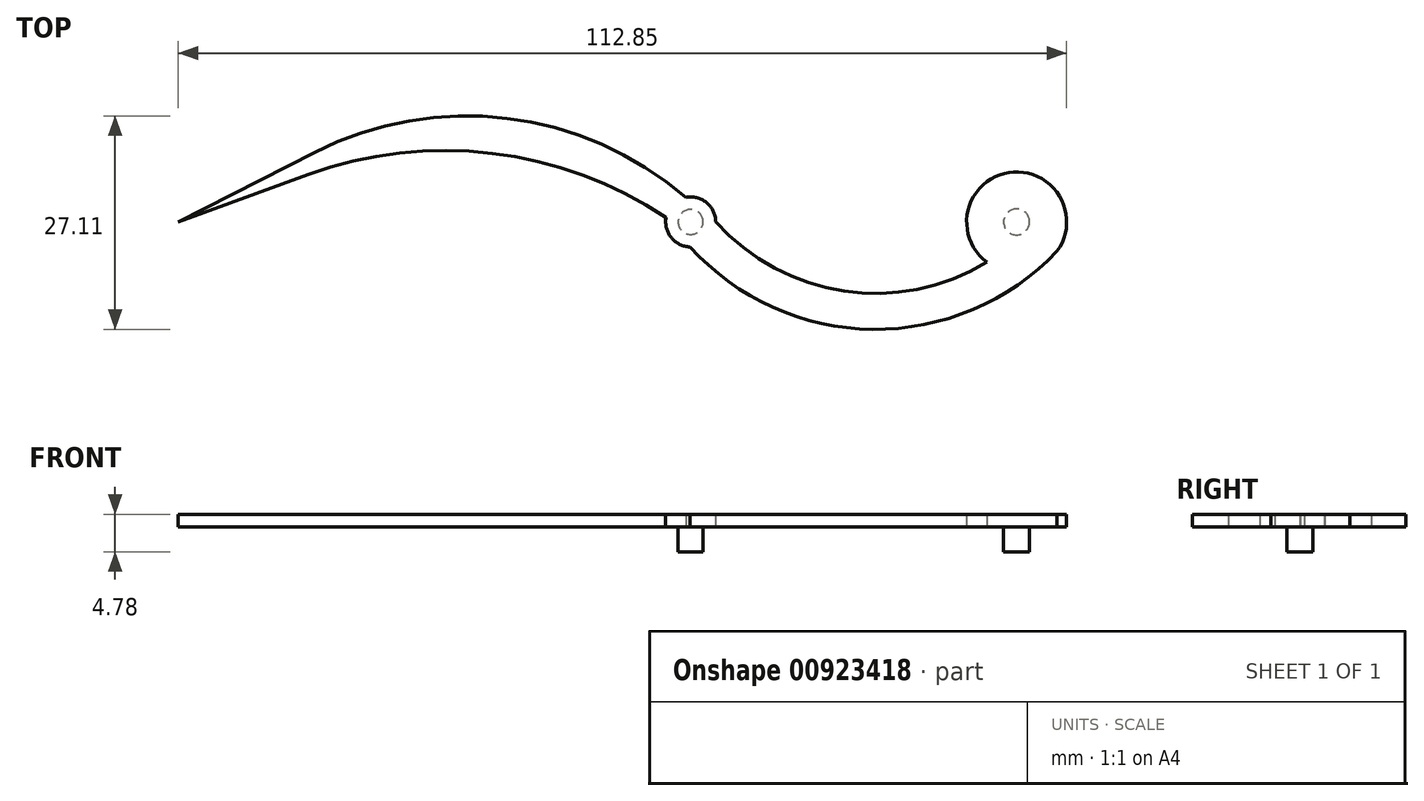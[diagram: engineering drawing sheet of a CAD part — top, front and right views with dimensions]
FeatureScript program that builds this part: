
annotation { "Feature Type Name" : "Feature", "Feature Type Description" : "" }
export const myFeature = defineFeature(function(context is Context, id is Id, definition is map)
    precondition{}
    {
        {
            var Q0;
            Q0=qCreatedBy(makeId("Top.planeOp"),FACE);
            var sketch = newSketch(context, id + "F0", { "sketchPlane" : qUnion([Q0])});
            skArc(sketch, "E0", {"start": v(-38.23, 0.04) * mm, "mid": v(-21.93, -8.78) * mm, "end": v(-3.77, -5.1) * mm});
            skArc(sketch, "E1", {"start": v(-41.48, -3.17) * mm, "mid": v(-18.29, -13.65) * mm, "end": v(5.15, -3.72) * mm});
            skArc(sketch, "E2", {"start": v(5.15, -3.72) * mm, "mid": v(-0.98, 6.27) * mm, "end": v(-3.77, -5.1) * mm});
            skLineSegment(sketch, "E3", {"start": v(-106.5, 0) * mm, "end": v(-89.19, 8.82) * mm});
            skLineSegment(sketch, "E4", {"start": v(-106.5, 0) * mm, "end": v(-90.02, 6) * mm});
            skLineSegment(sketch, "E5", {"start": v(-106.5, 0) * mm, "end": v(-87.48, 0) * mm, "construction": true});
            skArc(sketch, "E6", {"start": v(-44.53, 0.57) * mm, "mid": v(-66.63, 8.7) * mm, "end": v(-90.02, 6) * mm});
            skArc(sketch, "E7", {"start": v(-42.02, 3.11) * mm, "mid": v(-64.73, 13.16) * mm, "end": v(-89.19, 8.82) * mm});
            skArc(sketch, "E8", {"start": v(-38.23, 0.04) * mm, "mid": v(-39.4, 2.47) * mm, "end": v(-42.02, 3.11) * mm});
            skArc(sketch, "E9", {"start": v(-44.53, 0.57) * mm, "mid": v(-43.87, -2) * mm, "end": v(-41.48, -3.17) * mm});
            skLineSegment(sketch, "E10", {"start": v(-69.85, -29.13) * mm, "end": v(-72.64, -41.74) * mm, "construction": true});
            skCircle(sketch, "E11", {"center": v(-41.4, 0) * mm, "radius": 1.59 * mm});
            skCircle(sketch, "E12", {"center": v(0, 0) * mm, "radius": 1.65 * mm});
            skSolve(sketch);
        }
        {
            var Q0;
            Q0 = qSketchRegion(id + "F0", true);
            extrude(context, id + "F1", {"entities" : qUnion([Q0]), "depth" : 1.6 * mm, "offsetDistance" : 25.4 * mm});
        }
        {
            var Q0;
            Q0=makeQuery(id+"F1.opExtrude","CAP_FACE",FACE,{"disambiguationData":[OSD([sQuery(id+"F0.wireOp",EDGE,"E0"),sQuery(id+"F0.wireOp",EDGE,"E1"),sQuery(id+"F0.wireOp",EDGE,"E2"),sQuery(id+"F0.wireOp",EDGE,"E3"),sQuery(id+"F0.wireOp",EDGE,"E4"),sQuery(id+"F0.wireOp",EDGE,"E6"),sQuery(id+"F0.wireOp",EDGE,"E7"),sQuery(id+"F0.wireOp",EDGE,"E8"),sQuery(id+"F0.wireOp",EDGE,"E9"),sQuery(id+"F0.wireOp",EDGE,"E11"),sQuery(id+"F0.wireOp",EDGE,"E12")])],"isStart":false});
            var sketch = newSketch(context, id + "F2", { "sketchPlane" : qUnion([Q0])});
            skCircle(sketch, "E13", {"center": v(-41.4, 0) * mm, "radius": 1.59 * mm});
            skCircle(sketch, "E14", {"center": v(0, 0) * mm, "radius": 1.65 * mm});
            skSolve(sketch);
        }
        {
            var Q0;
            Q0 = qSketchRegion(id + "F2", true);
            extrude(context, id + "F3", {"entities" : qUnion([Q0]), "operationType" : NewBodyOperationType.ADD, "oppositeDirection" : true, "depth" : 4.78 * mm, "offsetDistance" : 25.4 * mm});
        }
    });
